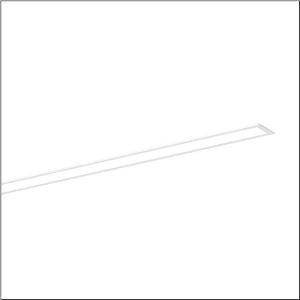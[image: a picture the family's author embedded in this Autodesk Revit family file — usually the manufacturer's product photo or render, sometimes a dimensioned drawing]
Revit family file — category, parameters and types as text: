
# Revit family: silica_r__21_51mx10tct5w_f343
name_source: partatom
category: Lighting Fixtures
units: mm (PartAtom-declared; Revit-internal decimal feet)

## family parameters
Cut with Voids When Loaded = No
Host = Face
Light Source = No
Part Type = Normal
Room Calculation Point = No
Round Connector Dimension = Use Diameter
Shared = No

## types (1)
- --- (1 x LED, 6000 lm, 51.3 W, 6500K)
    Apparent Load = 51 VA
    CIE Flux Codes = 48 79 96 100 100
    Color Rendering = 80
    Color Temperature = 6500K
    Default Elevation = 1800 mm
    Description = Silica® 21, office luminaire, primary optical cover: cover, of PMMA, opal, light emission: direct distribution, primary light characteristic: symmetric, installation type: recessed, LED, rated luminous flux: 6.000lm, luminous efficacy: 112lm/W, light colour: 8tw, colour temperature: 2700..6500K, with terminal, 3+2-pole, max. 2.5mm², mains connection: 220..240V, AC, 50/60Hz, rated input power: 53.8W, luminaire housing, of aluminium, traffic white (RAL 9016), length: 3.028mm, width: 79mm, height: 53mm, protection rating (complete): IP20, insulation class (complete): insulation class I (protective earthing), certification: CE, permissible operating ambient temperature: 0..+35°C, standard: EN 50419, packaging unit: 1 piece
    Height = 0 mm  [stored 0 ft]
    Lamp = 1 x LED
    Lamp Light Flux = 6000 lm
    Lamp Power = 51.3 W
    Lamp count = 1
    Length = 3027 mm
    Luminous efficacy = 117 lm/W
    Manufacturer = Siteco
    ModVariant = No
    Model = 51MX10TCT5W
    Mounting Place = Ceiling
    Mounting Type = Recessed
    Number of Poles = 1
    OnlyDefault = Yes
    Power Factor = 1
    Product Name = Silica® 21
    Product group = office luminaire | ceiling recessed
    ProductGroupID = 401
    Protection Class = Protection class I
    Protection Degree = IP 20
    RLX_Detail_Level = 1
    RLX_Emergency_Light_Flux = 0 lm
    RLX_Emergency_Type = 0
    RLX_Emergency_Type_DB = No
    RlxData = <blob elided: 17869 chars, md5=8eb7ffb1>
    Socket = socket
    Standby Power = 0 W
    System Light Flux = 6000 lm
    System Power = 51 W
    Type Comments = individual setting
    Type Image = l_1297737.jpg
    URL = http://relux.com
    VarID = @adj_071041
    Voltage = 0 V
    Weight = 0.00 kg
    Width = 79 mm

note: [stored X ft] marks values corroborated as IEEE doubles in the binary element streams (Revit-internal decimal feet)

## geometry (parser evidence)
native form markers: Blend x4, Sweep x9
no freeform markers — native parametric forms only
